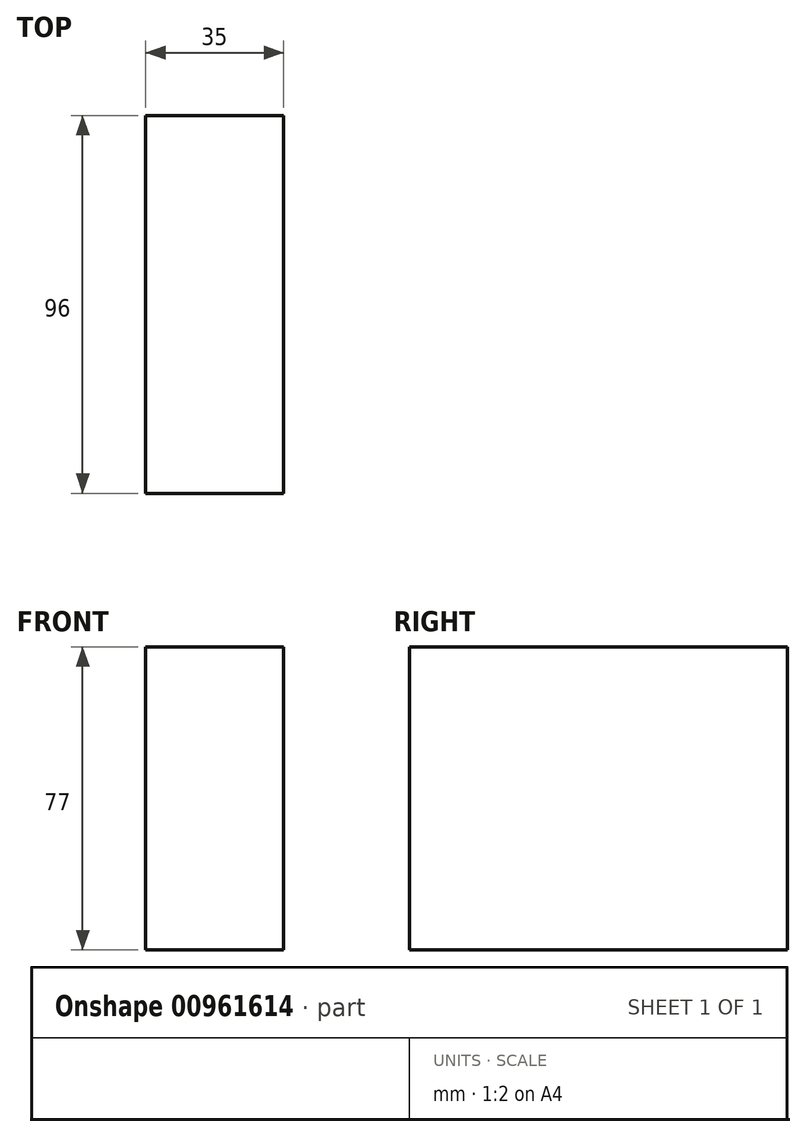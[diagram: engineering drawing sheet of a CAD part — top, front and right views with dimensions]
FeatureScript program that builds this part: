
annotation { "Feature Type Name" : "Feature", "Feature Type Description" : "" }
export const myFeature = defineFeature(function(context is Context, id is Id, definition is map)
    precondition{}
    {
        {
            var Q0;
            Q0=qCreatedBy(makeId("Top.planeOp"),FACE);
            var sketch = newSketch(context, id + "F0", { "sketchPlane" : qUnion([Q0])});
            skLineSegment(sketch, "E0.bottom", {"start": v(-17.85, 89.6) * mm, "end": v(17.15, 89.6) * mm});
            skLineSegment(sketch, "E0.top", {"start": v(-17.85, -6.4) * mm, "end": v(17.15, -6.4) * mm});
            skLineSegment(sketch, "E0.left", {"start": v(-17.85, 89.6) * mm, "end": v(-17.85, -6.4) * mm});
            skLineSegment(sketch, "E0.right", {"start": v(17.15, 89.6) * mm, "end": v(17.15, -6.4) * mm});
            skSolve(sketch);
        }
        {
            var Q0;
            Q0 = qSketchRegion(id + "F0", true);
            extrude(context, id + "F1", {"entities" : qUnion([Q0]), "depth" : 77 * mm, "offsetDistance" : 25 * mm});
        }
    });
